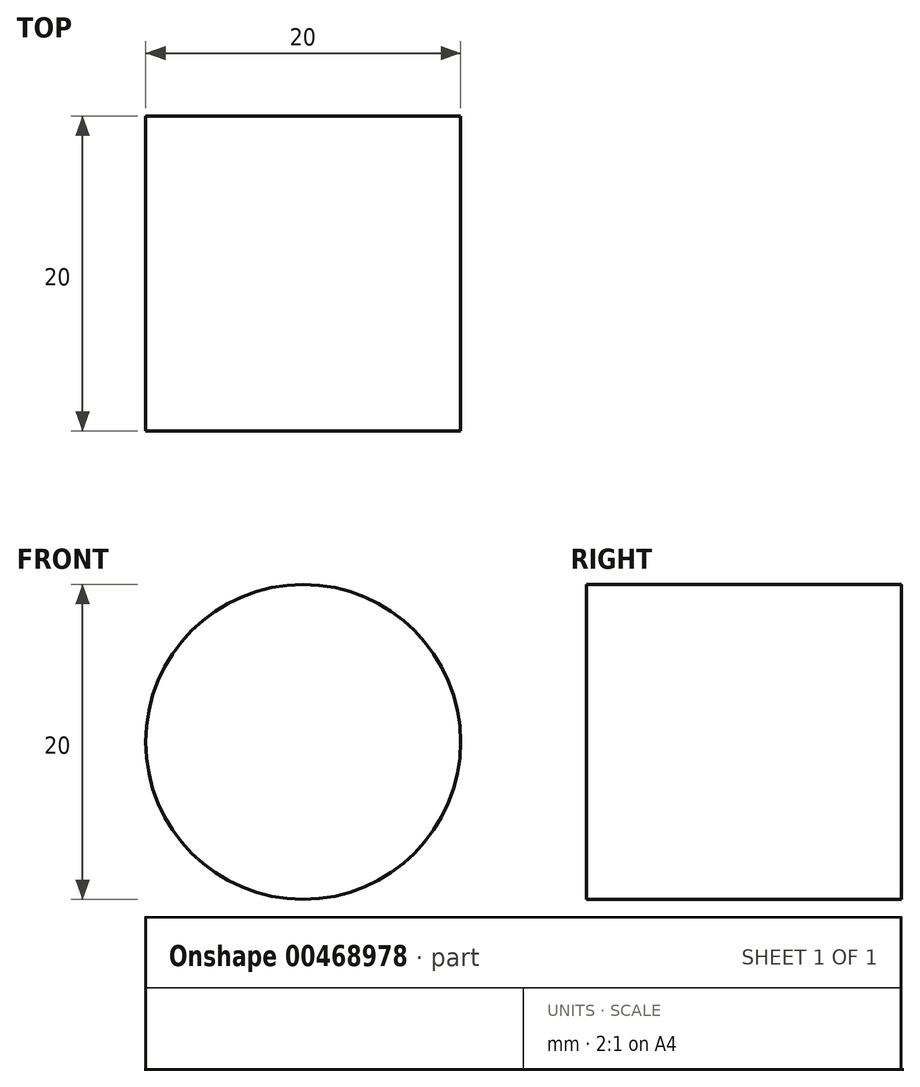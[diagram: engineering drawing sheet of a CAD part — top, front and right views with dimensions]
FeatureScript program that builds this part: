
annotation { "Feature Type Name" : "Feature", "Feature Type Description" : "" }
export const myFeature = defineFeature(function(context is Context, id is Id, definition is map)
    precondition{}
    {
        {
            var Q0;
            Q0=qCreatedBy(makeId("Front.planeOp"),FACE);
            var sketch = newSketch(context, id + "F0", { "sketchPlane" : qUnion([Q0])});
            skCircle(sketch, "E0", {"center": v(0, 0) * mm, "radius": 10 * mm});
            skSolve(sketch);
        }
        {
            var Q0;
            Q0 = qSketchRegion(id + "F0", true);
            extrude(context, id + "F1", {"entities" : qUnion([Q0]), "flatOperationType" : FlatOperationType.REMOVE, "offsetDistance" : 25 * mm, "depth" : 20 * mm, "domain" : OperationDomain.MODEL});
        }
    });
